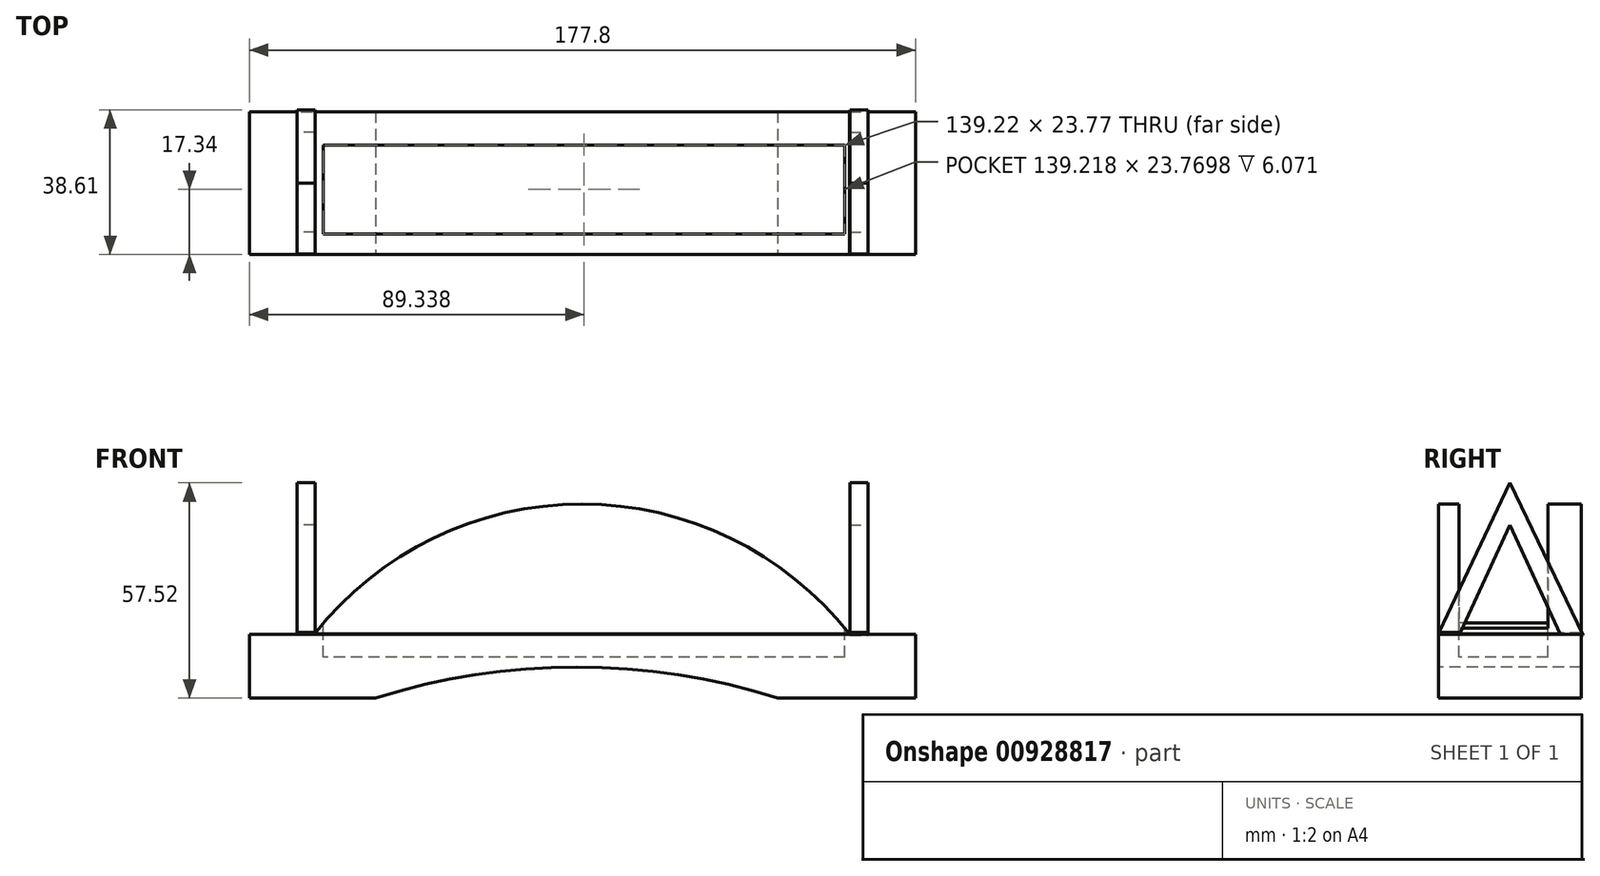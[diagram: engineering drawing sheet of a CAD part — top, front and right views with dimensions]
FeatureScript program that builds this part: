
annotation { "Feature Type Name" : "Feature", "Feature Type Description" : "" }
export const myFeature = defineFeature(function(context is Context, id is Id, definition is map)
    precondition{}
    {
        {
            var Q0;
            Q0=qCreatedBy(makeId("Top.planeOp"),FACE);
            var sketch = newSketch(context, id + "F0", { "sketchPlane" : qUnion([Q0])});
            skLineSegment(sketch, "E0.bottom", {"start": v(-88.9, 19.05) * mm, "end": v(88.9, 19.05) * mm});
            skLineSegment(sketch, "E0.top", {"start": v(-88.9, -19.05) * mm, "end": v(88.9, -19.05) * mm});
            skLineSegment(sketch, "E0.left", {"start": v(-88.9, 19.05) * mm, "end": v(-88.9, -19.05) * mm});
            skLineSegment(sketch, "E0.right", {"start": v(88.9, 19.05) * mm, "end": v(88.9, -19.05) * mm});
            skPoint(sketch, "E0.middle", {"position": v(0, 0) * mm});
            skSolve(sketch);
        }
        {
            var Q0;
            Q0=makeQuery(id+"F0.imprint","IMPRINT",FACE,{"disambiguationData":[TD([[makeQuery(id+"F0.imprint","IMPRINT",EDGE,{"derivedFrom":sQuery(id+"F0.wireOp",EDGE,"E0.bottom")}),-1.0]])]});
            extrude(context, id + "F1", {"entities" : qUnion([Q0]), "depth" : 5.6 * mm, "offsetDistance" : 25.4 * mm});
        }
        {
            var Q0;
            Q0=qCreatedBy(makeId("Right.planeOp"),FACE);
            cPlane(context, id + "F2", {"entities" : qUnion([Q0]), "cplaneType" : CPlaneType.OFFSET, "offset" : 76.2 * mm, "width" : 152.4 * mm, "height" : 152.4 * mm});
        }
        {
            var Q0;
            Q0=qCreatedBy(id+"F2.planeOp",FACE);
            var sketch = newSketch(context, id + "F3", { "sketchPlane" : qUnion([Q0])});
            skLineSegment(sketch, "E1", {"start": v(-18.98, 6.06) * mm, "end": v(0, 46.09) * mm});
            skLineSegment(sketch, "E2", {"start": v(0, 46.09) * mm, "end": v(19.56, 5.31) * mm});
            skLineSegment(sketch, "E3", {"start": v(19.56, 5.31) * mm, "end": v(13.65, 5.31) * mm});
            skLineSegment(sketch, "E4", {"start": v(-18.98, 6.06) * mm, "end": v(-13.15, 6.06) * mm});
            skLineSegment(sketch, "E5", {"start": v(-13.15, 6.06) * mm, "end": v(0, 34.81) * mm});
            skLineSegment(sketch, "E6", {"start": v(0, 34.81) * mm, "end": v(13.65, 5.31) * mm});
            skSolve(sketch);
        }
        {
            var Q0;
            Q0 = qSketchRegion(id + "F3", true);
            extrude(context, id + "F4", {"entities" : qUnion([Q0]), "operationType" : NewBodyOperationType.ADD, "oppositeDirection" : true, "depth" : 4.83 * mm, "offsetDistance" : 25.4 * mm});
        }
        {
            var Q0;
            Q0=makeQuery(id+"F1.opExtrude","SWEPT_BODY",BODY,{"disambiguationData":[OSD([sQuery(id+"F0.wireOp",EDGE,"E0.bottom"),sQuery(id+"F0.wireOp",EDGE,"E0.top"),sQuery(id+"F0.wireOp",EDGE,"E0.left"),sQuery(id+"F0.wireOp",EDGE,"E0.right")])]});
            var Q1;
            Q1=qCreatedBy(makeId("Right.planeOp"),FACE);
            mirror(context, id + "F5", {"operationType" : NewBodyOperationType.ADD, "entities" : qUnion([Q0]), "mirrorPlane" : qUnion([Q1])});
        }
        {
            var Q0;
            Q0=makeQuery(id+"F1.opExtrude","CAP_FACE",FACE,{"disambiguationData":[OSD([sQuery(id+"F0.wireOp",EDGE,"E0.bottom"),sQuery(id+"F0.wireOp",EDGE,"E0.top"),sQuery(id+"F0.wireOp",EDGE,"E0.left"),sQuery(id+"F0.wireOp",EDGE,"E0.right")])],"isStart":true});
            extrude(context, id + "F6", {"entities" : qUnion([Q0]), "operationType" : NewBodyOperationType.ADD, "depth" : 11.43 * mm, "offsetDistance" : 25.4 * mm});
        }
        {
            var Q0;
            {var subQ0=sQuery(id+"F0.wireOp",EDGE,"E0.top");Q0=makeQuery(id+"F6.boolean.opBoolean","MERGE",FACE,{"derivedFrom":[makeQuery(id+"F1.opExtrude","SWEPT_FACE",FACE,{"disambiguationData":[OSD([subQ0])]}),makeQuery(id+"F6.opExtrude","SWEPT_FACE",FACE,{"disambiguationData":[OSD([subQ0])]})]});}
            var sketch = newSketch(context, id + "F7", { "sketchPlane" : qUnion([Q0])});
            skArc(sketch, "E7", {"start": v(52.14, -11.43) * mm, "mid": v(-1.55, -3.1) * mm, "end": v(-55.24, -11.43) * mm});
            skLineSegment(sketch, "E8", {"start": v(-55.24, -11.43) * mm, "end": v(52.14, -11.43) * mm});
            skSolve(sketch);
        }
        {
            var Q0;
            Q0 = qSketchRegion(id + "F7", true);
            extrude(context, id + "F8", {"entities" : qUnion([Q0]), "operationType" : NewBodyOperationType.REMOVE, "oppositeDirection" : true, "depth" : 233.43 * mm, "offsetDistance" : 25.4 * mm});
        }
        {
            var Q0;
            {var subQ0=sQuery(id+"F0.wireOp",EDGE,"E0.top");Q0=makeQuery(id+"F6.boolean.opBoolean","MERGE",FACE,{"derivedFrom":[makeQuery(id+"F1.opExtrude","SWEPT_FACE",FACE,{"disambiguationData":[OSD([subQ0])]}),makeQuery(id+"F6.opExtrude","SWEPT_FACE",FACE,{"disambiguationData":[OSD([subQ0])]})]});}
            cPlane(context, id + "F9", {"entities" : qUnion([Q0]), "cplaneType" : CPlaneType.OFFSET, "offset" : 0 * mm, "width" : 152.4 * mm, "height" : 152.4 * mm});
        }
        {
            var Q0;
            Q0=qCreatedBy(id+"F9.planeOp",FACE);
            var sketch = newSketch(context, id + "F10", { "sketchPlane" : qUnion([Q0])});
            skLineSegment(sketch, "E9", {"start": v(71.23, 5.74) * mm, "end": v(-71.52, 5.74) * mm});
            skArc(sketch, "E10", {"start": v(71.23, 5.74) * mm, "mid": v(-0.15, 40.4) * mm, "end": v(-71.52, 5.74) * mm});
            skSolve(sketch);
        }
        {
            var Q0;
            Q0 = qSketchRegion(id + "F10", true);
            extrude(context, id + "F11", {"entities" : qUnion([Q0]), "operationType" : NewBodyOperationType.ADD, "oppositeDirection" : true, "depth" : 38.1 * mm, "offsetDistance" : 25.4 * mm});
        }
        {
            var Q0;
            Q0=makeQuery(id+"F1.opExtrude","CAP_FACE",FACE,{"disambiguationData":[OSD([sQuery(id+"F0.wireOp",EDGE,"E0.bottom"),sQuery(id+"F0.wireOp",EDGE,"E0.top"),sQuery(id+"F0.wireOp",EDGE,"E0.left"),sQuery(id+"F0.wireOp",EDGE,"E0.right")])],"isStart":false});
            cPlane(context, id + "F12", {"entities" : qUnion([Q0]), "cplaneType" : CPlaneType.OFFSET, "offset" : 45.24 * mm, "width" : 152.4 * mm, "height" : 152.4 * mm});
        }
        {
            var Q0;
            Q0=qCreatedBy(id+"F12.planeOp",FACE);
            var sketch = newSketch(context, id + "F13", { "sketchPlane" : qUnion([Q0])});
            skLineSegment(sketch, "E11.bottom", {"start": v(70.05, 10.18) * mm, "end": v(-69.17, 10.18) * mm});
            skLineSegment(sketch, "E11.top", {"start": v(70.05, -13.6) * mm, "end": v(-69.17, -13.6) * mm});
            skLineSegment(sketch, "E11.left", {"start": v(70.05, 10.18) * mm, "end": v(70.05, -13.6) * mm});
            skLineSegment(sketch, "E11.right", {"start": v(-69.17, 10.18) * mm, "end": v(-69.17, -13.6) * mm});
            skSolve(sketch);
        }
        {
            var Q0;
            Q0=makeQuery(id+"F13.imprint","IMPRINT",FACE,{"disambiguationData":[TD([[makeQuery(id+"F13.imprint","IMPRINT",EDGE,{"derivedFrom":sQuery(id+"F13.wireOp",EDGE,"E11.bottom")}),1.0]])]});
            extrude(context, id + "F14", {"entities" : qUnion([Q0]), "operationType" : NewBodyOperationType.REMOVE, "oppositeDirection" : true, "depth" : 51.3 * mm, "offsetDistance" : 25.4 * mm});
        }
    });
